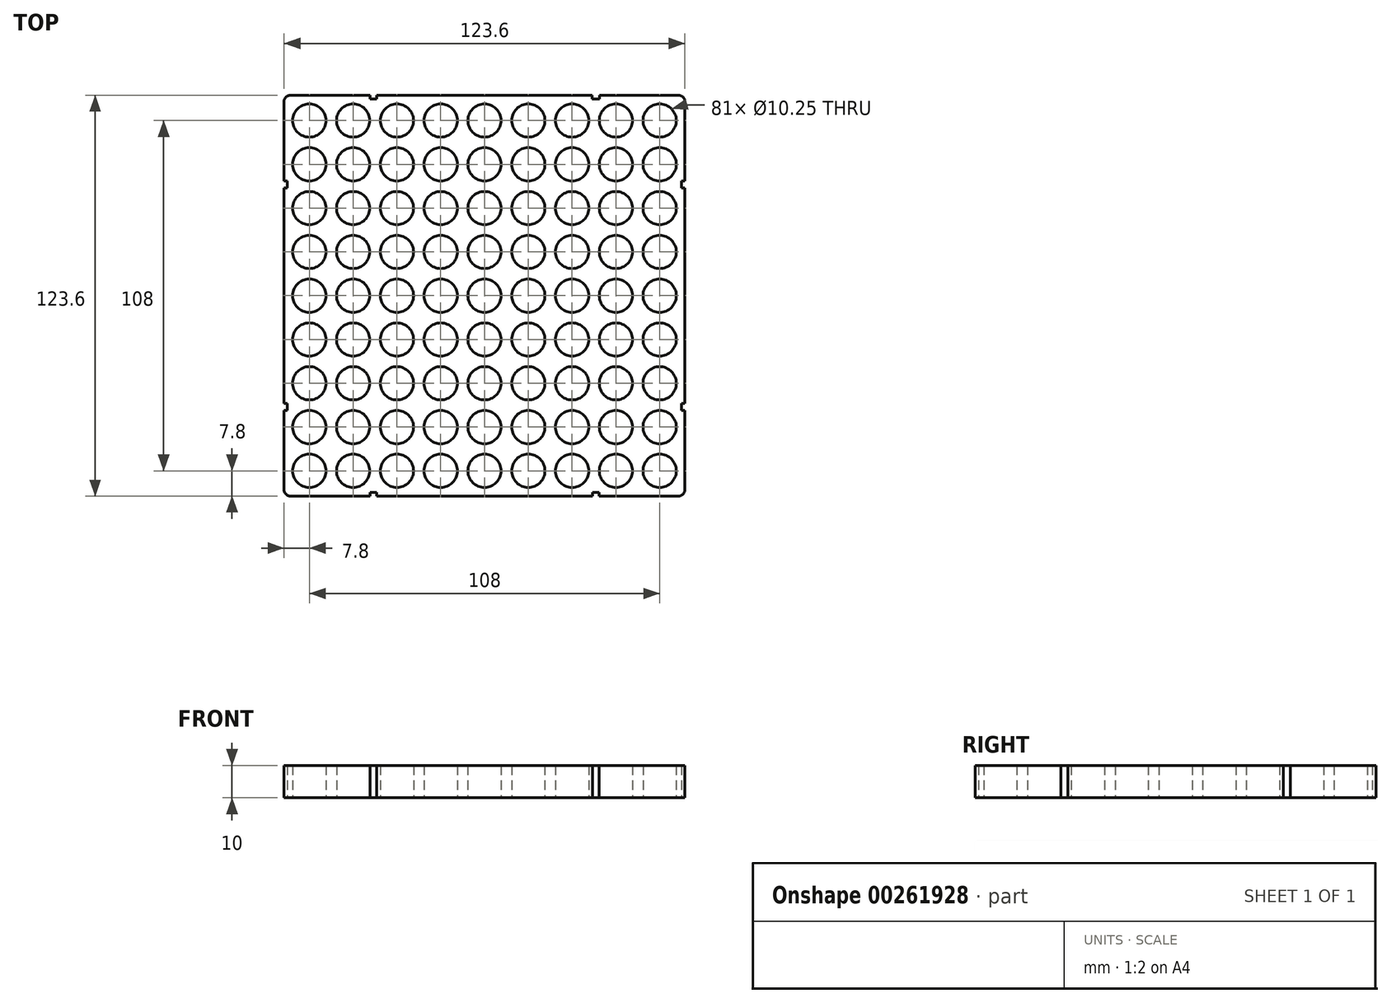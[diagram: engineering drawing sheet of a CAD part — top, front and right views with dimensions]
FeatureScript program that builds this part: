
annotation { "Feature Type Name" : "Feature", "Feature Type Description" : "" }
export const myFeature = defineFeature(function(context is Context, id is Id, definition is map)
    precondition{}
    {
        {
            var Q0;
            Q0=qCreatedBy(makeId("Top.planeOp"),FACE);
            var sketch = newSketch(context, id + "F0", { "sketchPlane" : qUnion([Q0])});
            skLineSegment(sketch, "E0.bottom", {"start": v(59.8, 61.8) * mm, "end": v(-59.8, 61.8) * mm});
            skLineSegment(sketch, "E0.top", {"start": v(59.8, -61.8) * mm, "end": v(-59.8, -61.8) * mm});
            skLineSegment(sketch, "E0.left", {"start": v(61.8, 59.8) * mm, "end": v(61.8, -59.8) * mm});
            skLineSegment(sketch, "E0.right", {"start": v(-61.8, 59.8) * mm, "end": v(-61.8, -59.8) * mm});
            skPoint(sketch, "E0.middle", {"position": v(0, 0) * mm});
            skPoint(sketch, "E1.visualSharp", {"position": v(-61.8, 61.8) * mm});
            skArc(sketch, "E1.filletArc", {"start": v(-59.8, 61.8) * mm, "mid": v(-61.21, 61.21) * mm, "end": v(-61.8, 59.8) * mm});
            skPoint(sketch, "E2.visualSharp", {"position": v(61.8, 61.8) * mm});
            skArc(sketch, "E2.filletArc", {"start": v(61.8, 59.8) * mm, "mid": v(61.21, 61.21) * mm, "end": v(59.8, 61.8) * mm});
            skPoint(sketch, "E3.visualSharp", {"position": v(61.8, -61.8) * mm});
            skArc(sketch, "E3.filletArc", {"start": v(59.8, -61.8) * mm, "mid": v(61.21, -61.21) * mm, "end": v(61.8, -59.8) * mm});
            skPoint(sketch, "E4.visualSharp", {"position": v(-61.8, -61.8) * mm});
            skArc(sketch, "E4.filletArc", {"start": v(-61.8, -59.8) * mm, "mid": v(-61.21, -61.21) * mm, "end": v(-59.8, -61.8) * mm});
            skLineSegment(sketch, "E5", {"start": v(-74.03, 0) * mm, "end": v(67.95, 0) * mm, "construction": true});
            skLineSegment(sketch, "E6", {"start": v(0, 65.94) * mm, "end": v(0, -57.14) * mm, "construction": true});
            skLineSegment(sketch, "E7", {"start": v(-13.5, 65.94) * mm, "end": v(-13.5, -57.14) * mm, "construction": true});
            skLineSegment(sketch, "E8", {"start": v(-27, 65.94) * mm, "end": v(-27, -57.14) * mm, "construction": true});
            skLineSegment(sketch, "E9", {"start": v(-40.5, 65.94) * mm, "end": v(-40.5, -57.14) * mm, "construction": true});
            skLineSegment(sketch, "E10", {"start": v(-54, 65.94) * mm, "end": v(-54, -57.14) * mm, "construction": true});
            skLineSegment(sketch, "E11", {"start": v(13.5, 65.94) * mm, "end": v(13.5, -57.14) * mm, "construction": true});
            skLineSegment(sketch, "E12", {"start": v(27, 65.94) * mm, "end": v(27, -57.14) * mm, "construction": true});
            skLineSegment(sketch, "E13", {"start": v(40.5, 65.94) * mm, "end": v(40.5, -57.14) * mm, "construction": true});
            skLineSegment(sketch, "E14", {"start": v(54, 65.94) * mm, "end": v(54, -57.14) * mm, "construction": true});
            skLineSegment(sketch, "E15", {"start": v(-74.03, 13.5) * mm, "end": v(67.95, 13.5) * mm, "construction": true});
            skLineSegment(sketch, "E16", {"start": v(-74.03, 27) * mm, "end": v(67.95, 27) * mm, "construction": true});
            skLineSegment(sketch, "E17", {"start": v(-74.03, 40.5) * mm, "end": v(67.95, 40.5) * mm, "construction": true});
            skLineSegment(sketch, "E18", {"start": v(-74.03, 54) * mm, "end": v(67.95, 54) * mm, "construction": true});
            skLineSegment(sketch, "E19", {"start": v(-74.03, -13.5) * mm, "end": v(67.95, -13.5) * mm, "construction": true});
            skLineSegment(sketch, "E20", {"start": v(-74.03, -27) * mm, "end": v(67.95, -27) * mm, "construction": true});
            skLineSegment(sketch, "E21", {"start": v(-74.03, -40.5) * mm, "end": v(67.95, -40.5) * mm, "construction": true});
            skLineSegment(sketch, "E22", {"start": v(-74.03, -54) * mm, "end": v(67.95, -54) * mm, "construction": true});
            skCircle(sketch, "E23", {"center": v(-54, 54) * mm, "radius": 5.12 * mm});
            skCircle(sketch, "E24", {"center": v(-54, 40.5) * mm, "radius": 5.12 * mm});
            skCircle(sketch, "E25", {"center": v(-40.5, 40.5) * mm, "radius": 5.12 * mm});
            skCircle(sketch, "E26", {"center": v(-40.5, 54) * mm, "radius": 5.12 * mm});
            skCircle(sketch, "E27", {"center": v(-27, 54) * mm, "radius": 5.12 * mm});
            skCircle(sketch, "E28", {"center": v(-27, 40.5) * mm, "radius": 5.12 * mm});
            skCircle(sketch, "E29", {"center": v(-13.5, 54) * mm, "radius": 5.12 * mm});
            skCircle(sketch, "E30", {"center": v(-13.5, 40.5) * mm, "radius": 5.12 * mm});
            skCircle(sketch, "E31", {"center": v(0, 54) * mm, "radius": 5.12 * mm});
            skCircle(sketch, "E32", {"center": v(0, 40.5) * mm, "radius": 5.12 * mm});
            skCircle(sketch, "E33", {"center": v(13.5, 40.5) * mm, "radius": 5.12 * mm});
            skCircle(sketch, "E34", {"center": v(13.5, 54) * mm, "radius": 5.12 * mm});
            skCircle(sketch, "E35", {"center": v(27, 54) * mm, "radius": 5.12 * mm});
            skCircle(sketch, "E36", {"center": v(27, 40.5) * mm, "radius": 5.12 * mm});
            skCircle(sketch, "E37", {"center": v(40.5, 54) * mm, "radius": 5.12 * mm});
            skCircle(sketch, "E38", {"center": v(40.5, 40.5) * mm, "radius": 5.12 * mm});
            skCircle(sketch, "E39", {"center": v(54, 54) * mm, "radius": 5.12 * mm});
            skCircle(sketch, "E40", {"center": v(54, 40.5) * mm, "radius": 5.12 * mm});
            skCircle(sketch, "E41", {"center": v(-54, 27) * mm, "radius": 5.12 * mm});
            skCircle(sketch, "E42", {"center": v(-40.5, 27) * mm, "radius": 5.12 * mm});
            skCircle(sketch, "E43", {"center": v(-27, 27) * mm, "radius": 5.12 * mm});
            skCircle(sketch, "E44", {"center": v(-13.5, 27) * mm, "radius": 5.12 * mm});
            skCircle(sketch, "E45", {"center": v(0, 27) * mm, "radius": 5.12 * mm});
            skCircle(sketch, "E46", {"center": v(13.5, 27) * mm, "radius": 5.12 * mm});
            skCircle(sketch, "E47", {"center": v(27, 27) * mm, "radius": 5.12 * mm});
            skCircle(sketch, "E48", {"center": v(40.5, 27) * mm, "radius": 5.12 * mm});
            skCircle(sketch, "E49", {"center": v(54, 27) * mm, "radius": 5.12 * mm});
            skCircle(sketch, "E50", {"center": v(-54, 13.5) * mm, "radius": 5.12 * mm});
            skCircle(sketch, "E51", {"center": v(-40.5, 13.5) * mm, "radius": 5.12 * mm});
            skCircle(sketch, "E52", {"center": v(-27, 13.5) * mm, "radius": 5.12 * mm});
            skCircle(sketch, "E53", {"center": v(-13.5, 13.5) * mm, "radius": 5.12 * mm});
            skCircle(sketch, "E54", {"center": v(0, 13.5) * mm, "radius": 5.12 * mm});
            skCircle(sketch, "E55", {"center": v(13.5, 13.5) * mm, "radius": 5.12 * mm});
            skCircle(sketch, "E56", {"center": v(27, 13.5) * mm, "radius": 5.12 * mm});
            skCircle(sketch, "E57", {"center": v(40.5, 13.5) * mm, "radius": 5.12 * mm});
            skCircle(sketch, "E58", {"center": v(54, 13.5) * mm, "radius": 5.12 * mm});
            skCircle(sketch, "E59", {"center": v(54, 0) * mm, "radius": 5.12 * mm});
            skCircle(sketch, "E60", {"center": v(54, -13.5) * mm, "radius": 5.12 * mm});
            skCircle(sketch, "E61", {"center": v(40.5, 0) * mm, "radius": 5.12 * mm});
            skCircle(sketch, "E62", {"center": v(40.5, -13.5) * mm, "radius": 5.12 * mm});
            skCircle(sketch, "E63", {"center": v(27, 0) * mm, "radius": 5.12 * mm});
            skCircle(sketch, "E64", {"center": v(27, -13.5) * mm, "radius": 5.12 * mm});
            skCircle(sketch, "E65", {"center": v(-54, 0) * mm, "radius": 5.12 * mm});
            skCircle(sketch, "E66", {"center": v(-40.5, 0) * mm, "radius": 5.12 * mm});
            skCircle(sketch, "E67", {"center": v(-27, 0) * mm, "radius": 5.12 * mm});
            skCircle(sketch, "E68", {"center": v(-13.5, 0) * mm, "radius": 5.12 * mm});
            skCircle(sketch, "E69", {"center": v(0, 0) * mm, "radius": 5.12 * mm});
            skCircle(sketch, "E70", {"center": v(13.5, 0) * mm, "radius": 5.12 * mm});
            skCircle(sketch, "E71", {"center": v(13.5, -13.5) * mm, "radius": 5.12 * mm});
            skCircle(sketch, "E72", {"center": v(-13.5, -13.5) * mm, "radius": 5.12 * mm});
            skCircle(sketch, "E73", {"center": v(0, -13.5) * mm, "radius": 5.12 * mm});
            skCircle(sketch, "E74", {"center": v(-27, -13.5) * mm, "radius": 5.12 * mm});
            skCircle(sketch, "E75", {"center": v(-54, -13.5) * mm, "radius": 5.12 * mm});
            skCircle(sketch, "E76", {"center": v(-40.5, -13.5) * mm, "radius": 5.12 * mm});
            skCircle(sketch, "E77", {"center": v(-54, -27) * mm, "radius": 5.12 * mm});
            skCircle(sketch, "E78", {"center": v(-54, -40.5) * mm, "radius": 5.12 * mm});
            skCircle(sketch, "E79", {"center": v(-54, -54) * mm, "radius": 5.12 * mm});
            skCircle(sketch, "E80", {"center": v(-40.5, -54) * mm, "radius": 5.12 * mm});
            skCircle(sketch, "E81", {"center": v(-40.5, -40.5) * mm, "radius": 5.12 * mm});
            skCircle(sketch, "E82", {"center": v(-40.5, -27) * mm, "radius": 5.12 * mm});
            skCircle(sketch, "E83", {"center": v(-27, -27) * mm, "radius": 5.12 * mm});
            skCircle(sketch, "E84", {"center": v(-27, -40.5) * mm, "radius": 5.12 * mm});
            skCircle(sketch, "E85", {"center": v(-27, -54) * mm, "radius": 5.12 * mm});
            skCircle(sketch, "E86", {"center": v(-13.5, -27) * mm, "radius": 5.12 * mm});
            skCircle(sketch, "E87", {"center": v(-13.5, -40.5) * mm, "radius": 5.12 * mm});
            skCircle(sketch, "E88", {"center": v(-13.5, -54) * mm, "radius": 5.12 * mm});
            skCircle(sketch, "E89", {"center": v(0, -27) * mm, "radius": 5.12 * mm});
            skCircle(sketch, "E90", {"center": v(0, -40.5) * mm, "radius": 5.12 * mm});
            skCircle(sketch, "E91", {"center": v(0, -54) * mm, "radius": 5.12 * mm});
            skCircle(sketch, "E92", {"center": v(13.5, -27) * mm, "radius": 5.12 * mm});
            skCircle(sketch, "E93", {"center": v(13.5, -40.5) * mm, "radius": 5.12 * mm});
            skCircle(sketch, "E94", {"center": v(13.5, -54) * mm, "radius": 5.12 * mm});
            skCircle(sketch, "E95", {"center": v(27, -27) * mm, "radius": 5.12 * mm});
            skCircle(sketch, "E96", {"center": v(27, -40.5) * mm, "radius": 5.12 * mm});
            skCircle(sketch, "E97", {"center": v(27, -54) * mm, "radius": 5.12 * mm});
            skCircle(sketch, "E98", {"center": v(40.5, -27) * mm, "radius": 5.12 * mm});
            skCircle(sketch, "E99", {"center": v(40.5, -40.5) * mm, "radius": 5.12 * mm});
            skCircle(sketch, "E100", {"center": v(40.5, -54) * mm, "radius": 5.12 * mm});
            skCircle(sketch, "E101", {"center": v(54, -27) * mm, "radius": 5.12 * mm});
            skCircle(sketch, "E102", {"center": v(54, -40.5) * mm, "radius": 5.12 * mm});
            skCircle(sketch, "E103", {"center": v(54, -54) * mm, "radius": 5.12 * mm});
            skSolve(sketch);
        }
        {
            var Q0;
            Q0=qCreatedBy(makeId("Top.planeOp"),FACE);
            var sketch = newSketch(context, id + "F1", { "sketchPlane" : qUnion([Q0])});
            skLineSegment(sketch, "E104", {"start": v(-34.3, 79.9) * mm, "end": v(-34.3, -79.91) * mm, "construction": true});
            skLineSegment(sketch, "E105", {"start": v(34.3, -79.91) * mm, "end": v(34.3, 79.84) * mm, "construction": true});
            skLineSegment(sketch, "E106", {"start": v(-79.51, 34.3) * mm, "end": v(79.76, 34.3) * mm, "construction": true});
            skLineSegment(sketch, "E107", {"start": v(-79.78, -34.3) * mm, "end": v(79.98, -34.3) * mm, "construction": true});
            skLineSegment(sketch, "E108.bottom", {"start": v(-33.3, 62.9) * mm, "end": v(-35.3, 62.9) * mm});
            skLineSegment(sketch, "E108.top", {"start": v(-33.3, 60.7) * mm, "end": v(-35.3, 60.7) * mm});
            skLineSegment(sketch, "E108.left", {"start": v(-33.3, 62.9) * mm, "end": v(-33.3, 60.7) * mm});
            skLineSegment(sketch, "E108.right", {"start": v(-35.3, 62.9) * mm, "end": v(-35.3, 60.7) * mm});
            skPoint(sketch, "E108.middle", {"position": v(-34.3, 61.8) * mm});
            skLineSegment(sketch, "E109.bottom", {"start": v(35.4, 62.9) * mm, "end": v(33.2, 62.9) * mm});
            skLineSegment(sketch, "E109.top", {"start": v(35.4, 60.7) * mm, "end": v(33.2, 60.7) * mm});
            skLineSegment(sketch, "E109.left", {"start": v(35.4, 62.9) * mm, "end": v(35.4, 60.7) * mm});
            skLineSegment(sketch, "E109.right", {"start": v(33.2, 62.9) * mm, "end": v(33.2, 60.7) * mm});
            skPoint(sketch, "E109.middle", {"position": v(34.3, 61.8) * mm});
            skLineSegment(sketch, "E110.bottom", {"start": v(62.9, 33.2) * mm, "end": v(60.7, 33.2) * mm});
            skLineSegment(sketch, "E110.top", {"start": v(62.9, 35.4) * mm, "end": v(60.7, 35.4) * mm});
            skLineSegment(sketch, "E110.left", {"start": v(62.9, 33.2) * mm, "end": v(62.9, 35.4) * mm});
            skLineSegment(sketch, "E110.right", {"start": v(60.7, 33.2) * mm, "end": v(60.7, 35.4) * mm});
            skPoint(sketch, "E110.middle", {"position": v(61.8, 34.3) * mm});
            skLineSegment(sketch, "E111.bottom", {"start": v(62.9, -35.4) * mm, "end": v(60.7, -35.4) * mm});
            skLineSegment(sketch, "E111.top", {"start": v(62.9, -33.2) * mm, "end": v(60.7, -33.2) * mm});
            skLineSegment(sketch, "E111.left", {"start": v(62.9, -35.4) * mm, "end": v(62.9, -33.2) * mm});
            skLineSegment(sketch, "E111.right", {"start": v(60.7, -35.4) * mm, "end": v(60.7, -33.2) * mm});
            skPoint(sketch, "E111.middle", {"position": v(61.8, -34.3) * mm});
            skLineSegment(sketch, "E112.bottom", {"start": v(35.3, -62.9) * mm, "end": v(33.3, -62.9) * mm});
            skLineSegment(sketch, "E112.top", {"start": v(35.3, -60.7) * mm, "end": v(33.3, -60.7) * mm});
            skLineSegment(sketch, "E112.left", {"start": v(35.3, -62.9) * mm, "end": v(35.3, -60.7) * mm});
            skLineSegment(sketch, "E112.right", {"start": v(33.3, -62.9) * mm, "end": v(33.3, -60.7) * mm});
            skPoint(sketch, "E112.middle", {"position": v(34.3, -61.8) * mm});
            skLineSegment(sketch, "E113.bottom", {"start": v(-33.3, -62.9) * mm, "end": v(-35.3, -62.9) * mm});
            skLineSegment(sketch, "E113.top", {"start": v(-33.3, -60.7) * mm, "end": v(-35.3, -60.7) * mm});
            skLineSegment(sketch, "E113.left", {"start": v(-33.3, -62.9) * mm, "end": v(-33.3, -60.7) * mm});
            skLineSegment(sketch, "E113.right", {"start": v(-35.3, -62.9) * mm, "end": v(-35.3, -60.7) * mm});
            skPoint(sketch, "E113.middle", {"position": v(-34.3, -61.8) * mm});
            skLineSegment(sketch, "E114.bottom", {"start": v(-60.8, -33.2) * mm, "end": v(-62.8, -33.2) * mm});
            skLineSegment(sketch, "E114.top", {"start": v(-60.8, -35.4) * mm, "end": v(-62.8, -35.4) * mm});
            skLineSegment(sketch, "E114.left", {"start": v(-60.8, -33.2) * mm, "end": v(-60.8, -35.4) * mm});
            skLineSegment(sketch, "E114.right", {"start": v(-62.8, -33.2) * mm, "end": v(-62.8, -35.4) * mm});
            skPoint(sketch, "E114.middle", {"position": v(-61.8, -34.3) * mm});
            skLineSegment(sketch, "E115.bottom", {"start": v(-60.8, 35.4) * mm, "end": v(-62.8, 35.4) * mm});
            skLineSegment(sketch, "E115.top", {"start": v(-60.8, 33.2) * mm, "end": v(-62.8, 33.2) * mm});
            skLineSegment(sketch, "E115.left", {"start": v(-60.8, 35.4) * mm, "end": v(-60.8, 33.2) * mm});
            skLineSegment(sketch, "E115.right", {"start": v(-62.8, 35.4) * mm, "end": v(-62.8, 33.2) * mm});
            skPoint(sketch, "E115.middle", {"position": v(-61.8, 34.3) * mm});
            skSolve(sketch);
        }
        {
            var Q0;
            Q0=makeQuery(id+"F0.imprint","IMPRINT",FACE,{"disambiguationData":[TD([[makeQuery(id+"F0.imprint","IMPRINT",EDGE,{"derivedFrom":sQuery(id+"F0.wireOp",EDGE,"E0.bottom")}),1.0]])]});
            extrude(context, id + "F2", {"entities" : qUnion([Q0]), "depth" : 10 * mm});
        }
        {
            var Q0;
            Q0 = qSketchRegion(id + "F1", true);
            extrude(context, id + "F3", {"entities" : qUnion([Q0]), "operationType" : NewBodyOperationType.REMOVE, "depth" : 10 * mm});
        }
    });
